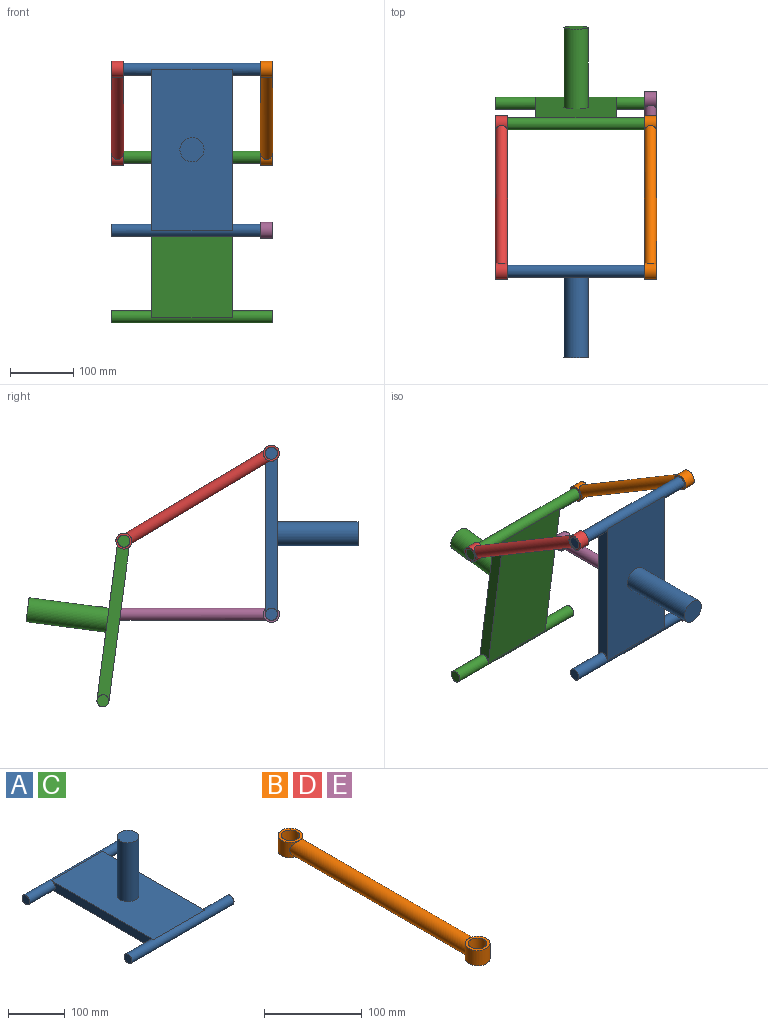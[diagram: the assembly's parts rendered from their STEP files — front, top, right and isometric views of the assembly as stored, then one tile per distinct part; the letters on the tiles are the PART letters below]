
ASSEMBLY  parts=5 mates=7
PART A: 12 faces, bbox 254x273.1x146.1 mm
  f0: plane 254x19.05mm, normal (-1,0,0), area 4553.7mm2, adj f2,f3,f4,f7
  f1: plane 254x19.05mm, normal (1,0,0), area 4553.7mm2, adj f2,f3,f4,f7
  f2: plane 254x127mm, normal (0,0,1), area 31117.9mm2, adj f0,f1,f4,f7,f10
  f3: plane 254x127mm, normal (0,0,-1), area 32258mm2, adj f0,f1,f4,f7
  f4: cylinder r=9.53mm len=254mm, axis (-1,0,0), area 11400.9mm2, adj f0,f1,f2,f3,f5,f6
  f5: plane 19.05x19.05mm, normal (1,0,0), area 285mm2, adj f4
  f6: plane 19.05x19.05mm, normal (-1,0,0), area 285mm2, adj f4
  f7: cylinder r=9.53mm len=254mm, axis (-1,0,0), area 11400.9mm2, adj f0,f1,f2,f3,f8,f9
  f8: plane 19.05x19.05mm, normal (1,0,0), area 285mm2, adj f7
  f9: plane 19.05x19.05mm, normal (-1,0,0), area 285mm2, adj f7
  f10: cylinder r=19.05mm len=127mm, axis (0,0,-1), area 15201.2mm2, adj f2,f11
  f11: plane 38.1x38.1mm, normal (0,0,1), area 1140.1mm2, adj f10
PART B: 9 faces, bbox 25.4x296.2x19.1 mm
  f0: plane 25.4x25.4mm, normal (0,0,1), area 221.7mm2, adj f2,f4
  f1: plane 25.4x25.4mm, normal (0,0,-1), area 221.7mm2, adj f2,f4
  f2: cylinder r=12.7mm len=25.4mm, axis (0,0,-1), area 1208.9mm2, adj f0,f1,f8
  f3: cylinder r=12.7mm len=25.4mm, axis (0,0,-1), area 1208.9mm2, adj f6,f7,f8
  f4: cylinder r=9.53mm len=19.05mm, axis (0,0,-1), area 1140.1mm2, adj f0,f1
  f5: cylinder r=9.53mm len=19.05mm, axis (0,0,-1), area 1140.1mm2, adj f6,f7
  f6: plane 25.4x25.4mm, normal (0,0,1), area 221.7mm2, adj f3,f5
  f7: plane 25.4x25.4mm, normal (0,0,-1), area 221.7mm2, adj f3,f5
  f8: cylinder r=9.53mm len=254mm, axis (0,-1,0), area 14930.8mm2, adj f2,f3
PART C: same geometry as A
PART D: same geometry as B
PART E: same geometry as B
PLACE A rot(axis=(1,0,0),90deg) t=(-303.13,9.53,-15.63)mm
PLACE B rot(axis=(-0.26,-0.93,0.26),94deg) t=(0,0,0)mm
PLACE C rot(axis=(-1,0,0),82.5deg) t=(-303.13,254.11,-376.27)mm
PLACE D rot(axis=(-0.26,-0.93,0.26),94deg) t=(-234.95,0,0)mm
PLACE E rot(axis=(0,-1,0),90deg) t=(0,0,-254)mm
MATE revolute E.f4 <-> A.f7  axis (1,0,0) through (0,0,-254)mm
MATE cylindrical C.f7 <-> B.f5  axis (1,0,0) through (0,232.6,-138.68)mm
MATE planar D.f5 <-> C.f7  axis (-1,0,0) through (-254,232.6,-138.68)mm
MATE revolute D.f4 <-> A.f4  axis (1,0,0) through (-254,0,0)mm
MATE parallel B.f5 <-> C.f7  axis (1,0,0) through (0,232.6,-138.68)mm
MATE revolute B.f4 <-> A.f4  axis (1,0,0) through (0,0,0)mm
MATE cylindrical C.f7 <-> D.f5  axis (-1,0,0) through (-254,232.6,-138.68)mm
